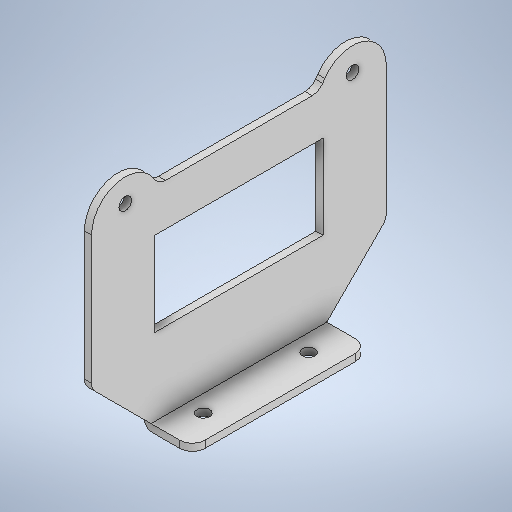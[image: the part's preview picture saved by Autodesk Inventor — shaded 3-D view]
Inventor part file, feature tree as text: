
AUTODESK INVENTOR PART (.ipt)
format: ipt  version: 2025.2 (Build 292293000, 293)  size: 324,608 bytes
history: native  units: mm
features: fillet x4, extrude x3, sketch x3
ambient origin geometry x8: Origin, YZ Plane, XZ Plane, XY Plane, X Axis, Y Axis, Z Axis, Center Point
bodies: Solid1 (feature_tree)
feature tree (10):
  extrude  "Extrusion1"  Depth=3.0mm
  extrude  "Extrusion2"  Depth=3.0mm
  extrude  "Extrusion3"  Depth=40.0mm
  fillet  "Fillet1"  Radius=20.0mm
  fillet  "Fillet2"  Radius=30.0mm
  fillet  "Fillet3"  Radius=3.0mm
  fillet  "Fillet4"  Radius=3.0mm
  sketch  "Sketch1"  dims[d0=12.5mm d1=3.0mm]
  sketch  "Sketch2"  dims[d2=3.0mm d3=3.0mm]
  sketch  "Sketch3"  dims[d4=1.7mm d5=0.0mm d6=40.0mm d7=20.0mm d8=30.0mm d9=3.0mm d10=3.0mm d11=50.0mm d12=50.0mm d13=54.0mm d14=27.0mm d15=20.0mm d16=45.0deg d17=40.0mm d18=90.0deg d19=20.0mm d20=135.0deg d21=40.0mm d22=1.7mm d23=0.0mm d24=10.0mm d25=4.0mm d26=4.0mm d27=4.0mm d28=4.0mm d29=10.0mm d30=0.0mm d31=8.0mm d32=3.0mm d33=3.0mm d34=2.0mm]
